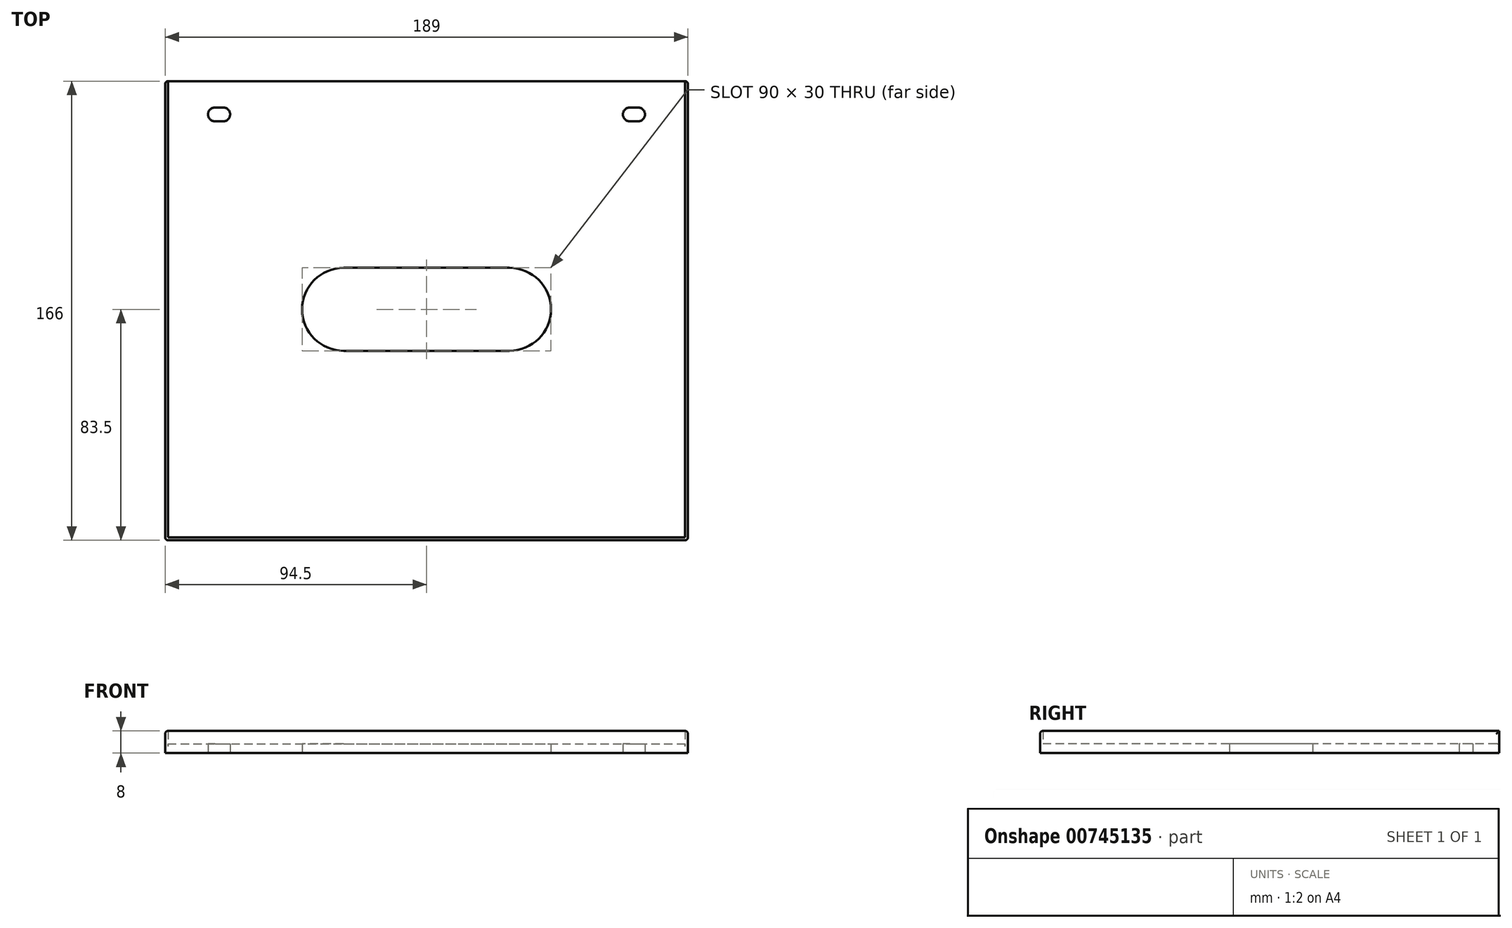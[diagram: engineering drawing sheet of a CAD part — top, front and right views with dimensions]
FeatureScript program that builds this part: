
annotation { "Feature Type Name" : "Feature", "Feature Type Description" : "" }
export const myFeature = defineFeature(function(context is Context, id is Id, definition is map)
    precondition{}
    {
        {
            var Q0;
            Q0=qCreatedBy(makeId("Top.planeOp"),FACE);
            var sketch = newSketch(context, id + "F0", { "sketchPlane" : qUnion([Q0])});
            skLineSegment(sketch, "E0.bottom", {"start": v(-93.5, 82.5) * mm, "end": v(93.5, 82.5) * mm});
            skLineSegment(sketch, "E0.top", {"start": v(-93.5, -82.5) * mm, "end": v(93.5, -82.5) * mm});
            skLineSegment(sketch, "E0.left", {"start": v(-93.5, 82.5) * mm, "end": v(-93.5, -82.5) * mm});
            skLineSegment(sketch, "E0.right", {"start": v(93.5, 82.5) * mm, "end": v(93.5, -82.5) * mm});
            skPoint(sketch, "E0.middle", {"position": v(0, 0) * mm});
            skLineSegment(sketch, "E1", {"start": v(-76.5, 70.5) * mm, "end": v(-73.5, 70.5) * mm});
            skArc(sketch, "E2.0.startCap", {"start": v(-76.5, 68) * mm, "mid": v(-79, 70.5) * mm, "end": v(-76.5, 73) * mm});
            skArc(sketch, "E2.0.endCap", {"start": v(-73.5, 73) * mm, "mid": v(-71, 70.5) * mm, "end": v(-73.5, 68) * mm});
            skLineSegment(sketch, "E2.0.left", {"start": v(-76.5, 73) * mm, "end": v(-73.5, 73) * mm});
            skLineSegment(sketch, "E2.0.right", {"start": v(-76.5, 68) * mm, "end": v(-73.5, 68) * mm});
            skLineSegment(sketch, "E3", {"start": v(73.5, 70.5) * mm, "end": v(76.5, 70.5) * mm});
            skArc(sketch, "E4.0.startCap", {"start": v(73.5, 68) * mm, "mid": v(71, 70.5) * mm, "end": v(73.5, 73) * mm});
            skArc(sketch, "E4.0.endCap", {"start": v(76.5, 73) * mm, "mid": v(79, 70.5) * mm, "end": v(76.5, 68) * mm});
            skLineSegment(sketch, "E4.0.left", {"start": v(73.5, 73) * mm, "end": v(76.5, 73) * mm});
            skLineSegment(sketch, "E4.0.right", {"start": v(73.5, 68) * mm, "end": v(76.5, 68) * mm});
            skLineSegment(sketch, "E5.0", {"start": v(94.5, 82.5) * mm, "end": v(94.5, -83.5) * mm});
            skLineSegment(sketch, "E5.1", {"start": v(-94.5, -83.5) * mm, "end": v(94.5, -83.5) * mm});
            skLineSegment(sketch, "E5.2", {"start": v(-94.5, 82.5) * mm, "end": v(-94.5, -83.5) * mm});
            skLineSegment(sketch, "E6", {"start": v(-94.5, 82.5) * mm, "end": v(-93.5, 82.5) * mm});
            skLineSegment(sketch, "E7", {"start": v(93.5, 82.5) * mm, "end": v(94.5, 82.5) * mm});
            skLineSegment(sketch, "E8", {"start": v(-30, 0) * mm, "end": v(30, 0) * mm});
            skArc(sketch, "E9.0.startCap", {"start": v(-30, -15) * mm, "mid": v(-45, 0) * mm, "end": v(-30, 15) * mm});
            skArc(sketch, "E9.0.endCap", {"start": v(30, 15) * mm, "mid": v(45, 0) * mm, "end": v(30, -15) * mm});
            skLineSegment(sketch, "E9.0.left", {"start": v(-30, 15) * mm, "end": v(30, 15) * mm});
            skLineSegment(sketch, "E9.0.right", {"start": v(-30, -15) * mm, "end": v(30, -15) * mm});
            skSolve(sketch);
        }
        {
            var Q0;
            Q0=makeQuery(id+"F0.imprint","IMPRINT",FACE,{"disambiguationData":[TD([[makeQuery(id+"F0.imprint","IMPRINT",EDGE,{"derivedFrom":sQuery(id+"F0.wireOp",EDGE,"E0.top")}),-1.0]])]});
            extrude(context, id + "F1", {"entities" : qUnion([Q0]), "depth" : 8 * mm, "offsetDistance" : 25 * mm});
        }
        {
            var Q0;
            Q0=makeQuery(id+"F0.imprint","IMPRINT",FACE,{"disambiguationData":[TD([[makeQuery(id+"F0.imprint","IMPRINT",EDGE,{"derivedFrom":sQuery(id+"F0.wireOp",EDGE,"E0.bottom")}),-1.0]])]});
            extrude(context, id + "F2", {"entities" : qUnion([Q0]), "operationType" : NewBodyOperationType.ADD, "depth" : 3.4 * mm, "offsetDistance" : 25 * mm});
        }
        {
            var Q0;
            Q0=makeQuery(id+"F1.opExtrude","SWEPT_EDGE",EDGE,{"disambiguationData":[OSD([sQuery(id+"F0.wireOp",EDGE,"E5.1"),sQuery(id+"F0.wireOp",EDGE,"E5.2")])]});
            var Q1;
            Q1=makeQuery(id+"F1.opExtrude","SWEPT_EDGE",EDGE,{"disambiguationData":[OSD([sQuery(id+"F0.wireOp",EDGE,"E5.0"),sQuery(id+"F0.wireOp",EDGE,"E5.1")])]});
            var Q2;
            Q2=makeQuery(id+"F1.opExtrude","SWEPT_EDGE",EDGE,{"disambiguationData":[OSD([sQuery(id+"F0.wireOp",EDGE,"E5.2"),sQuery(id+"F0.wireOp",EDGE,"E6")])]});
            var Q3;
            Q3=makeQuery(id+"F1.opExtrude","SWEPT_EDGE",EDGE,{"disambiguationData":[OSD([sQuery(id+"F0.wireOp",EDGE,"E5.0"),sQuery(id+"F0.wireOp",EDGE,"E7")])]});
            var Q4;
            Q4=makeQuery(id+"F1.opExtrude","CAP_EDGE",EDGE,{"disambiguationData":[OSD([sQuery(id+"F0.wireOp",EDGE,"E5.2")])],"isStart":false});
            var Q5;
            Q5=makeQuery(id+"F1.opExtrude","CAP_EDGE",EDGE,{"disambiguationData":[OSD([sQuery(id+"F0.wireOp",EDGE,"E5.1")])],"isStart":false});
            var Q6;
            Q6=makeQuery(id+"F1.opExtrude","CAP_EDGE",EDGE,{"disambiguationData":[OSD([sQuery(id+"F0.wireOp",EDGE,"E5.0")])],"isStart":false});
            fillet(context, id + "F3", {"entities" : qUnion([Q0, Q1, Q2, Q3, Q4, Q5, Q6]), "radius" : 1 * mm, "tangentPropagation" : true, "allowEdgeOverflow" : false});
        }
        {
            var Q0;
            Q0=makeQuery(id+"F2.opExtrude","CAP_EDGE",EDGE,{"disambiguationData":[OSD([sQuery(id+"F0.wireOp",EDGE,"E0.bottom")])],"isStart":false});
            fillet(context, id + "F4", {"entities" : qUnion([Q0]), "radius" : 1 * mm, "tangentPropagation" : true, "allowEdgeOverflow" : false});
        }
    });
